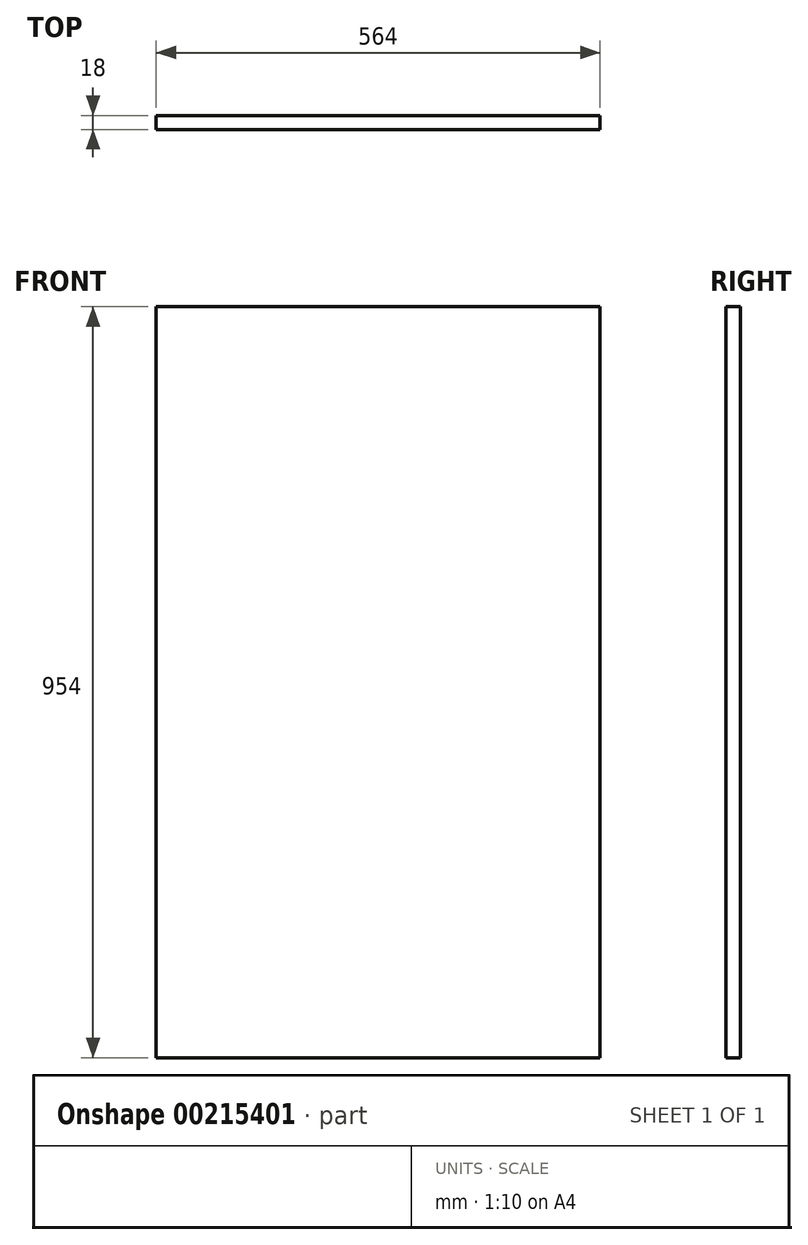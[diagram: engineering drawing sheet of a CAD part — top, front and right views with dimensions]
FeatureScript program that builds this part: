
annotation { "Feature Type Name" : "Feature", "Feature Type Description" : "" }
export const myFeature = defineFeature(function(context is Context, id is Id, definition is map)
    precondition{}
    {
        {
            var Q0;
            Q0=qCreatedBy(makeId("Front.planeOp"),FACE);
            var sketch = newSketch(context, id + "F0", { "sketchPlane" : qUnion([Q0])});
            skLineSegment(sketch, "E0.bottom", {"start": v(-282, -477) * mm, "end": v(282, -477) * mm});
            skLineSegment(sketch, "E0.top", {"start": v(-282, 477) * mm, "end": v(282, 477) * mm});
            skLineSegment(sketch, "E0.left", {"start": v(-282, -477) * mm, "end": v(-282, 477) * mm});
            skLineSegment(sketch, "E0.right", {"start": v(282, -477) * mm, "end": v(282, 477) * mm});
            skPoint(sketch, "E0.middle", {"position": v(0, 0) * mm});
            skSolve(sketch);
        }
        {
            var Q0;
            Q0=makeQuery(id+"F0.imprint","IMPRINT",FACE,{"disambiguationData":[TD([[makeQuery(id+"F0.imprint","IMPRINT",EDGE,{"derivedFrom":sQuery(id+"F0.wireOp",EDGE,"E0.bottom")}),1.0]])]});
            extrude(context, id + "F1", {"entities" : qUnion([Q0]), "depth" : 18 * mm});
        }
    });
